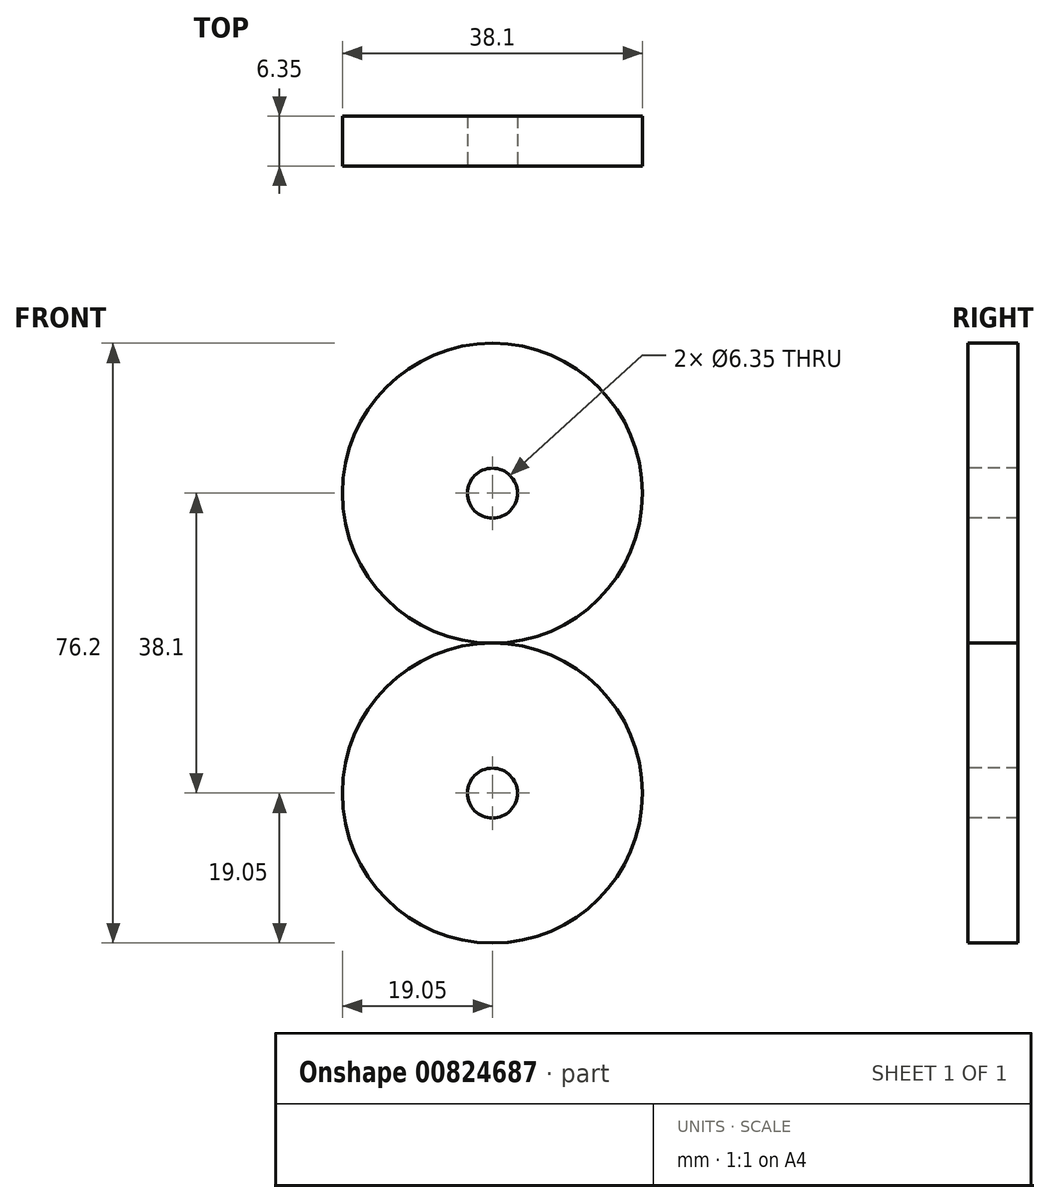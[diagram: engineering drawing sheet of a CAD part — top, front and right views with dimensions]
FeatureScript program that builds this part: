
annotation { "Feature Type Name" : "Feature", "Feature Type Description" : "" }
export const myFeature = defineFeature(function(context is Context, id is Id, definition is map)
    precondition{}
    {
        {
            var Q0;
            Q0=qCreatedBy(makeId("Front.planeOp"),FACE);
            var sketch = newSketch(context, id + "F0", { "sketchPlane" : qUnion([Q0])});
            skCircle(sketch, "E0", {"center": v(0, 0) * mm, "radius": 19.05 * mm});
            skCircle(sketch, "E1", {"center": v(0, 38.1) * mm, "radius": 19.05 * mm});
            skSolve(sketch);
        }
        {
            var Q0;
            Q0=qSketchRegion(id+"F0",true);
            extrude(context, id + "F1", {"entities" : qUnion([Q0]), "depth" : 6.35 * mm, "offsetDistance" : 25.4 * mm});
        }
        {
            var Q0;
            Q0=makeQuery(id+"F1.opExtrude","CAP_FACE",FACE,{"disambiguationData":[OSD([sQuery(id+"F0.wireOp",EDGE,"E0")])],"isStart":false});
            var sketch = newSketch(context, id + "F2", { "sketchPlane" : qUnion([Q0])});
            skCircle(sketch, "E2", {"center": v(0, 0) * mm, "radius": 3.18 * mm});
            skSolve(sketch);
        }
        {
            var Q0;
            Q0=makeQuery(id+"F1.opExtrude","CAP_FACE",FACE,{"disambiguationData":[OSD([sQuery(id+"F0.wireOp",EDGE,"E1")])],"isStart":false});
            var sketch = newSketch(context, id + "F3", { "sketchPlane" : qUnion([Q0])});
            skLineSegment(sketch, "E3", {"start": v(0, 57.15) * mm, "end": v(0, 38.1) * mm});
            skCircle(sketch, "E4", {"center": v(0, 38.1) * mm, "radius": 3.18 * mm});
            skSolve(sketch);
        }
        {
            var Q0;
            Q0=makeQuery(id+"F3.imprint","IMPRINT",FACE,{"disambiguationData":[TD([[makeQuery(id+"F3.imprint","IMPRINT",EDGE,{"derivedFrom":sQuery(id+"F3.wireOp",EDGE,"E4")}),1.0]])]});
            var Q1;
            Q1=makeQuery(id+"F2.imprint","IMPRINT",FACE,{"disambiguationData":[TD([[makeQuery(id+"F2.imprint","IMPRINT",EDGE,{"derivedFrom":sQuery(id+"F2.wireOp",EDGE,"E2")}),1.0]])]});
            extrude(context, id + "F4", {"entities" : qUnion([Q0, Q1]), "operationType" : NewBodyOperationType.REMOVE, "oppositeDirection" : true, "depth" : 6.35 * mm, "offsetDistance" : 25.4 * mm});
        }
    });
